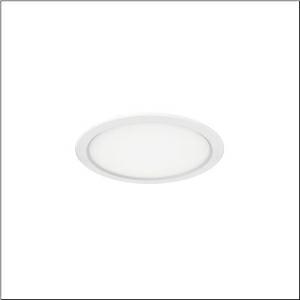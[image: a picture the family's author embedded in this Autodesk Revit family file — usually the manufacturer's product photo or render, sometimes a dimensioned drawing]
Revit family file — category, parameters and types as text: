
# Revit family: lunis_41_eco_51ds107f34b
name_source: partatom
category: Lighting Fixtures
units: mm (PartAtom-declared; Revit-internal decimal feet)

## family parameters
Cut with Voids When Loaded = No
Host = Face
Light Source = No
Part Type = Normal
Room Calculation Point = No
Round Connector Dimension = Use Diameter
Shared = No

## types (1)
- Lunis 41 Eco (1 x LED, 2150 lm, 17.5 W, 3000K)
    Apparent Load = 18 VA
    CIE Flux Codes = 47 80 97 100 100
    Color Rendering = 80
    Color Temperature = 3000K
    Default Elevation = 1800 mm
    Description = Lunis 41 Eco, downlight, light emission: direct distribution, LED rated luminous flux: 2.150lm, light colour: 830, mains connection: 230V, AC, 50/60Hz, housing, round, of aluminium, coated, traffic white (RAL 9016), diameter: 216mm, recess depth: 58mm, protection rating (complete): IP20, protection rating (on room side): IP40, insulation class (complete): insulation class II (safety insulation), certification: CE, permissible ambient temperature for indoor applications: -20..+40°C, packaging unit: 1 piece
    Height = 0 mm  [stored 0 ft]
    Lamp = 1 x LED
    Lamp Light Flux = 2150 lm
    Lamp Power = 17.5 W
    Lamp count = 1
    Length = 216 mm
    Luminous efficacy = 123 lm/W
    Manufacturer = Siteco
    ModVariant = No
    Model = 51DS107F34B
    Mounting Place = Ceiling
    Mounting Type = Recessed
    Number of Poles = 1
    OnlyDefault = Yes
    Power Factor = 1
    Product Name = Lunis 41 Eco
    Product group = downlight
    ProductGroupID = 401
    Protection Class = Protection class II
    Protection Degree = IP 20
    RLX_Detail_Level = 1
    RLX_Emergency_Light_Flux = 0 lm
    RLX_Emergency_Type = 0
    RLX_Emergency_Type_DB = No
    RlxData = <blob elided: 10221 chars, md5=b912dcda>
    Socket = socket
    Standby Power = 0 W
    System Light Flux = 2150 lm
    System Power = 18 W
    Type Comments = Product without accessories
    Type Image = l_1345914.jpg
    URL = http://relux.com
    VarID = ---
    Voltage = 0 V
    Weight = 0.00 kg
    Width = 0 mm  [stored 0 ft]

note: [stored X ft] marks values corroborated as IEEE doubles in the binary element streams (Revit-internal decimal feet)

## geometry (parser evidence)
native form markers: Sweep x10
no freeform markers — native parametric forms only
